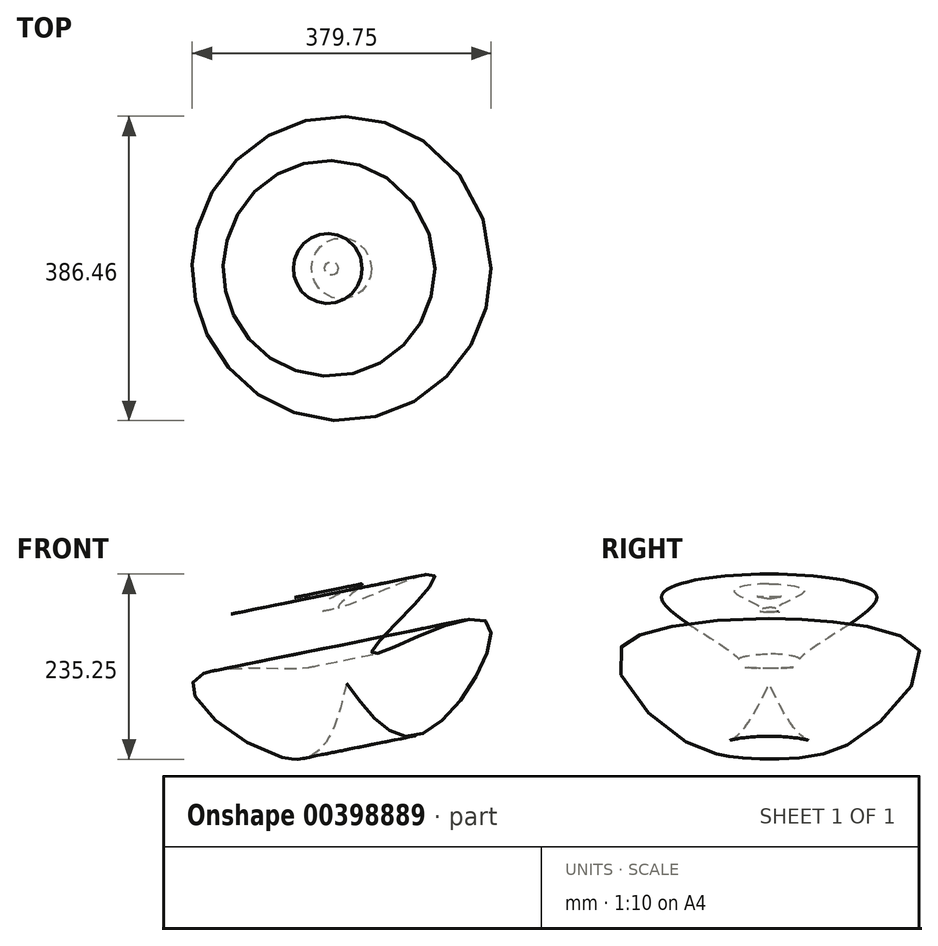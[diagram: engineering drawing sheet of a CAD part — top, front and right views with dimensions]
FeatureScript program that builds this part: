
annotation { "Feature Type Name" : "Feature", "Feature Type Description" : "" }
export const myFeature = defineFeature(function(context is Context, id is Id, definition is map)
    precondition{}
    {
        {
            var Q0;
            Q0=qCreatedBy(makeId("Front.planeOp"),FACE);
            var sketch = newSketch(context, id + "F0", { "sketchPlane" : qUnion([Q0])});
            skLineSegment(sketch, "E0", {"start": v(-61.69, 62.2) * mm, "end": v(-39.83, -45.7) * mm});
            skFitSpline(sketch, "E1", {"points": [v(-61.69, 62.2) * mm, v(-20.44, 79.4) * mm, v(-50.4, 51.01) * mm, v(71.9, 91.96) * mm, v(-8.1, -6.92) * mm, v(135.7, 34.6) * mm, v(59.57, -107.94) * mm, v(-39.83, -45.7) * mm], "startDerivative": vector(731.5, 365.35) * mm, "endDerivative": vector(-592.66, 805.46) * mm});
            skSolve(sketch);
        }
        {
            var Q0;
            Q0=makeQuery(id+"F0.imprint","IMPRINT",FACE,{"disambiguationData":[TD([[makeQuery(id+"F0.imprint","IMPRINT",EDGE,{"derivedFrom":sQuery(id+"F0.wireOp",EDGE,"E0")}),1.0]])]});
            var Q1;
            Q1=sQuery(id+"F0.wireOp",EDGE,"E0");
            revolve(context, id + "F1", {"entities" : qUnion([Q0]), "axis" : qUnion([Q1]), "revolveType" : RevolveType.FULL});
        }
    });
